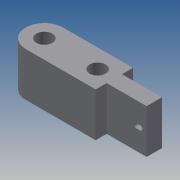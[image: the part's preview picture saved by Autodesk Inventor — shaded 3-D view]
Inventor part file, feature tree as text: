
AUTODESK INVENTOR PART (.ipt)
format: ipt  version: 2013 (Build 170138000, 138)  size: 128,512 bytes
history: native  units: mm
features: extrude x4, sketch x4
ambient origin geometry x8: Origin, YZ Plane, XZ Plane, XY Plane, X Axis, Y Axis, Z Axis, Center Point
bodies: Solid1 (feature_tree)
feature tree (8):
  extrude  "Extrusion1"  Depth=30.0mm
  extrude  "Extrusion2"  Depth=11.5mm
  extrude  "Extrusion3"  Depth=12.0mm
  extrude  "Extrusion4"  Depth=33.0mm TaperAngle=0.0deg
  sketch  "Sketch1"  dims[d0=82.5mm d1=30.0mm]
  sketch  "Sketch2"  dims[d2=14.0mm d3=11.5mm]
  sketch  "Sketch3"  dims[d4=33.0mm d5=0.0mm d6=12.0mm]
  sketch  "Sketch4"  dims[d8=40.0mm d9=33.0mm d10=0.0mm d11=3.0mm d13=5.0mm d14=1.75mm d15=10.0mm d16=0.0mm d17=5.0mm d18=7.0mm d19=3.5mm d20=8.0mm d21=0.5mm d22=1.0mm d23=1.5mm d24=2.0mm d25=2.5mm d26=3.0mm d27=10.0mm d28=0.0mm]
